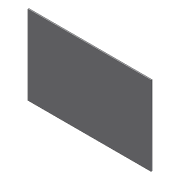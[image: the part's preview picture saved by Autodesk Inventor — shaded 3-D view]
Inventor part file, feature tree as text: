
AUTODESK INVENTOR PART (.ipt)
format: ipt  version: 2012 (Build 160160000, 160)  size: 66,048 bytes
history: native  units: in
note: dims shown in document units (in); Inventor stores cm internally (conversion verified against a paired STEP export)
features: extrude x1, sketch x1
ambient origin geometry x8: Origin, YZ Plane, XZ Plane, XY Plane, X Axis, Y Axis, Z Axis, Center Point
bodies: Solid1 (feature_tree)
feature tree (2):
  extrude  "Extrusion1"  Depth=25.0in
  sketch  "Sketch1"  dims[d0=25.0in d1=25.0in d2=16.0in d3=0.25in d4=0.0in]
